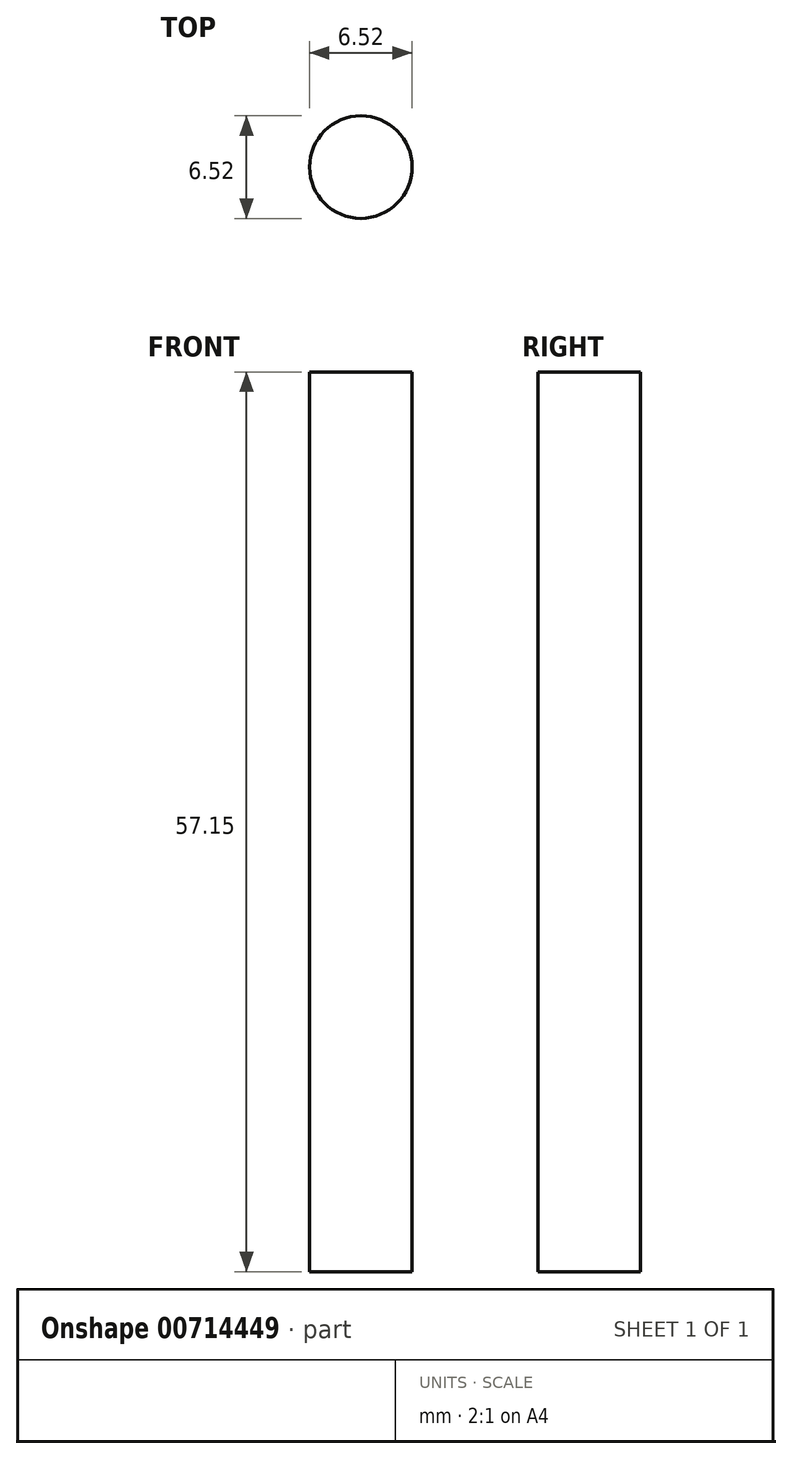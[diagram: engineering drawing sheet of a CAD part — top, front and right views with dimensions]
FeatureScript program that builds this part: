
annotation { "Feature Type Name" : "Feature", "Feature Type Description" : "" }
export const myFeature = defineFeature(function(context is Context, id is Id, definition is map)
    precondition{}
    {
        {
            var Q0;
            Q0=qCreatedBy(makeId("Top.planeOp"),FACE);
            var sketch = newSketch(context, id + "F0", { "sketchPlane" : qUnion([Q0])});
            skCircle(sketch, "E0", {"center": v(0, 0) * mm, "radius": 3.26 * mm});
            skSolve(sketch);
        }
        {
            var Q0;
            Q0=makeQuery(id+"F0.imprint","IMPRINT",FACE,{"disambiguationData":[TD([[makeQuery(id+"F0.imprint","IMPRINT",EDGE,{"derivedFrom":sQuery(id+"F0.wireOp",EDGE,"E0")}),1.0]])]});
            extrude(context, id + "F1", {"entities" : qUnion([Q0]), "depth" : 57.15 * mm});
        }
    });
